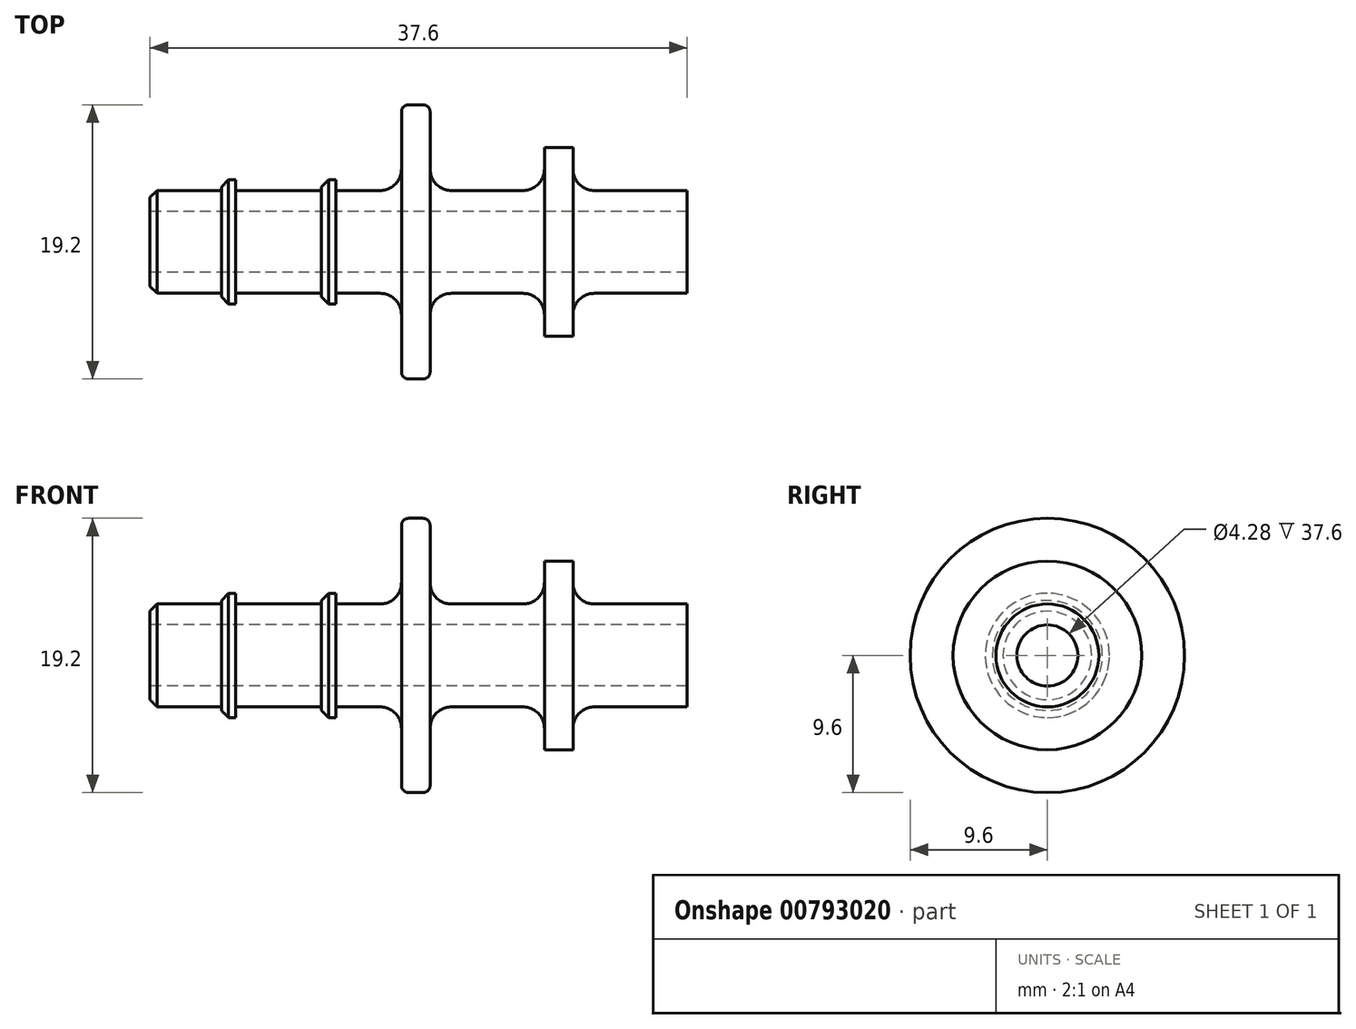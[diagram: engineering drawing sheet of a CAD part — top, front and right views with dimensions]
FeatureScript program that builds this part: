
annotation { "Feature Type Name" : "Feature", "Feature Type Description" : "" }
export const myFeature = defineFeature(function(context is Context, id is Id, definition is map)
    precondition{}
    {
        {
            var Q0;
            Q0=qCreatedBy(makeId("Front.planeOp"),FACE);
            var sketch = newSketch(context, id + "F0", { "sketchPlane" : qUnion([Q0])});
            skLineSegment(sketch, "E0.bottom", {"start": v(-18.8, 0) * mm, "end": v(18.8, 0) * mm});
            skLineSegment(sketch, "E0.top", {"start": v(-18.8, 0) * mm, "end": v(18.8, 0) * mm});
            skLineSegment(sketch, "E0.left", {"start": v(-18.8, 0) * mm, "end": v(-18.8, 0) * mm});
            skLineSegment(sketch, "E0.right", {"start": v(18.8, 0) * mm, "end": v(18.8, 0) * mm});
            skPoint(sketch, "E0.middle", {"position": v(0, 0) * mm});
            skLineSegment(sketch, "E1", {"start": v(18.8, 0) * mm, "end": v(18.8, 3.6) * mm});
            skLineSegment(sketch, "E2", {"start": v(18.8, 3.6) * mm, "end": v(12.3, 3.6) * mm});
            skLineSegment(sketch, "E3", {"start": v(10.8, 5.1) * mm, "end": v(10.8, 6.6) * mm});
            skLineSegment(sketch, "E4", {"start": v(10.8, 6.6) * mm, "end": v(8.8, 6.6) * mm});
            skLineSegment(sketch, "E5", {"start": v(8.8, 6.6) * mm, "end": v(8.8, 5.1) * mm});
            skLineSegment(sketch, "E6", {"start": v(7.3, 3.6) * mm, "end": v(2.3, 3.6) * mm});
            skLineSegment(sketch, "E7", {"start": v(0.8, 5.1) * mm, "end": v(0.8, 9.1) * mm});
            skLineSegment(sketch, "E8", {"start": v(0.3, 9.6) * mm, "end": v(-0.7, 9.6) * mm});
            skLineSegment(sketch, "E9", {"start": v(-1.2, 9.1) * mm, "end": v(-1.2, 5.1) * mm});
            skLineSegment(sketch, "E10", {"start": v(-2.7, 3.6) * mm, "end": v(-5.8, 3.6) * mm});
            skLineSegment(sketch, "E11", {"start": v(-5.8, 3.6) * mm, "end": v(-5.8, 4.35) * mm});
            skLineSegment(sketch, "E12", {"start": v(-5.8, 4.35) * mm, "end": v(-6.8, 4.35) * mm});
            skLineSegment(sketch, "E13", {"start": v(-6.8, 4.35) * mm, "end": v(-6.8, 3.6) * mm});
            skLineSegment(sketch, "E14", {"start": v(-6.8, 3.6) * mm, "end": v(-12.8, 3.6) * mm});
            skLineSegment(sketch, "E15", {"start": v(-12.8, 3.6) * mm, "end": v(-12.8, 4.35) * mm});
            skLineSegment(sketch, "E16", {"start": v(-12.8, 4.35) * mm, "end": v(-13.8, 4.35) * mm});
            skLineSegment(sketch, "E17", {"start": v(-13.8, 4.35) * mm, "end": v(-13.8, 3.6) * mm});
            skLineSegment(sketch, "E18", {"start": v(-13.8, 3.6) * mm, "end": v(-18.8, 3.6) * mm});
            skLineSegment(sketch, "E19", {"start": v(-18.8, 3.6) * mm, "end": v(-18.8, 0) * mm});
            skPoint(sketch, "E20.visualSharp", {"position": v(0.8, 9.6) * mm});
            skArc(sketch, "E20.filletArc", {"start": v(0.8, 9.1) * mm, "mid": v(0.65, 9.45) * mm, "end": v(0.3, 9.6) * mm});
            skPoint(sketch, "E21.visualSharp", {"position": v(-1.2, 9.6) * mm});
            skArc(sketch, "E21.filletArc", {"start": v(-0.7, 9.6) * mm, "mid": v(-1.05, 9.45) * mm, "end": v(-1.2, 9.1) * mm});
            skPoint(sketch, "E22.visualSharp", {"position": v(0.8, 3.6) * mm});
            skArc(sketch, "E22.filletArc", {"start": v(0.8, 5.1) * mm, "mid": v(1.24, 4.04) * mm, "end": v(2.3, 3.6) * mm});
            skPoint(sketch, "E23.visualSharp", {"position": v(-1.2, 3.6) * mm});
            skArc(sketch, "E23.filletArc", {"start": v(-2.7, 3.6) * mm, "mid": v(-1.64, 4.04) * mm, "end": v(-1.2, 5.1) * mm});
            skPoint(sketch, "E24.visualSharp", {"position": v(10.8, 3.6) * mm});
            skArc(sketch, "E24.filletArc", {"start": v(10.8, 5.1) * mm, "mid": v(11.24, 4.04) * mm, "end": v(12.3, 3.6) * mm});
            skPoint(sketch, "E25.visualSharp", {"position": v(8.8, 3.6) * mm});
            skArc(sketch, "E25.filletArc", {"start": v(7.3, 3.6) * mm, "mid": v(8.36, 4.04) * mm, "end": v(8.8, 5.1) * mm});
            skLineSegment(sketch, "E26.MirrorCS", {"start": v(18.8, 0) * mm, "end": v(18.8, -3.6) * mm});
            skLineSegment(sketch, "E27.MirrorCS", {"start": v(18.8, -3.6) * mm, "end": v(12.3, -3.6) * mm});
            skArc(sketch, "E28.MirrorCS", {"start": v(10.8, -5.1) * mm, "mid": v(11.24, -4.04) * mm, "end": v(12.3, -3.6) * mm});
            skLineSegment(sketch, "E29.MirrorCS", {"start": v(10.8, -5.1) * mm, "end": v(10.8, -6.6) * mm});
            skLineSegment(sketch, "E30.MirrorCS", {"start": v(10.8, -6.6) * mm, "end": v(8.8, -6.6) * mm});
            skLineSegment(sketch, "E31.MirrorCS", {"start": v(8.8, -6.6) * mm, "end": v(8.8, -5.1) * mm});
            skArc(sketch, "E32.MirrorCS", {"start": v(7.3, -3.6) * mm, "mid": v(8.36, -4.04) * mm, "end": v(8.8, -5.1) * mm});
            skLineSegment(sketch, "E33.MirrorCS", {"start": v(7.3, -3.6) * mm, "end": v(2.3, -3.6) * mm});
            skArc(sketch, "E34.MirrorCS", {"start": v(0.8, -5.1) * mm, "mid": v(1.24, -4.04) * mm, "end": v(2.3, -3.6) * mm});
            skLineSegment(sketch, "E35.MirrorCS", {"start": v(0.8, -5.1) * mm, "end": v(0.8, -9.1) * mm});
            skArc(sketch, "E36.MirrorCS", {"start": v(0.8, -9.1) * mm, "mid": v(0.65, -9.45) * mm, "end": v(0.3, -9.6) * mm});
            skLineSegment(sketch, "E37.MirrorCS", {"start": v(0.3, -9.6) * mm, "end": v(-0.7, -9.6) * mm});
            skArc(sketch, "E38.MirrorCS", {"start": v(-0.7, -9.6) * mm, "mid": v(-1.05, -9.45) * mm, "end": v(-1.2, -9.1) * mm});
            skLineSegment(sketch, "E39.MirrorCS", {"start": v(-1.2, -9.1) * mm, "end": v(-1.2, -5.1) * mm});
            skArc(sketch, "E40.MirrorCS", {"start": v(-2.7, -3.6) * mm, "mid": v(-1.64, -4.04) * mm, "end": v(-1.2, -5.1) * mm});
            skLineSegment(sketch, "E41.MirrorCS", {"start": v(-2.7, -3.6) * mm, "end": v(-5.8, -3.6) * mm});
            skLineSegment(sketch, "E42.MirrorCS", {"start": v(-5.8, -3.6) * mm, "end": v(-5.8, -4.35) * mm});
            skLineSegment(sketch, "E43.MirrorCS", {"start": v(-5.8, -4.35) * mm, "end": v(-6.8, -4.35) * mm});
            skLineSegment(sketch, "E44.MirrorCS", {"start": v(-6.8, -4.35) * mm, "end": v(-6.8, -3.6) * mm});
            skLineSegment(sketch, "E45.MirrorCS", {"start": v(-6.8, -3.6) * mm, "end": v(-12.8, -3.6) * mm});
            skLineSegment(sketch, "E46.MirrorCS", {"start": v(-12.8, -3.6) * mm, "end": v(-12.8, -4.35) * mm});
            skLineSegment(sketch, "E47.MirrorCS", {"start": v(-12.8, -4.35) * mm, "end": v(-13.8, -4.35) * mm});
            skLineSegment(sketch, "E48.MirrorCS", {"start": v(-13.8, -4.35) * mm, "end": v(-13.8, -3.6) * mm});
            skLineSegment(sketch, "E49.MirrorCS", {"start": v(-13.8, -3.6) * mm, "end": v(-18.8, -3.6) * mm});
            skLineSegment(sketch, "E50.MirrorCS", {"start": v(-18.8, -3.6) * mm, "end": v(-18.8, 0) * mm});
            skLineSegment(sketch, "E51", {"start": v(-18.8, 2.14) * mm, "end": v(18.8, 2.14) * mm});
            skLineSegment(sketch, "E52", {"start": v(-18.8, -2.36) * mm, "end": v(18.8, -2.36) * mm});
            skSolve(sketch);
        }
        {
            var Q0;
            {var subQ3=sQuery(id+"F0.wireOp",EDGE,"E2");Q0=makeQuery(id+"F0.imprint","IMPRINT",FACE,{"disambiguationData":[TD([[makeQuery(id+"F0.imprint","IMPRINT",EDGE,{"derivedFrom":subQ3}),1.0]])]});}
            var Q1;
            Q1=sQuery(id+"F0.wireOp",EDGE,"E0.top");
            revolve(context, id + "F1", {"surfaceOperationType" : NewSurfaceOperationType.NEW, "entities" : qUnion([Q0]), "axis" : qUnion([Q1]), "revolveType" : RevolveType.FULL});
        }
        {
            var Q0;
            Q0=makeQuery(id+"F1.opRevolve","SWEPT_EDGE",EDGE,{"disambiguationData":[OSD([sQuery(id+"F0.wireOp",EDGE,"E18"),sQuery(id+"F0.wireOp",EDGE,"E19")])]});
            var Q1;
            Q1=makeQuery(id+"F1.opRevolve","SWEPT_EDGE",EDGE,{"disambiguationData":[OSD([sQuery(id+"F0.wireOp",EDGE,"E16"),sQuery(id+"F0.wireOp",EDGE,"E17")])]});
            var Q2;
            Q2=makeQuery(id+"F1.opRevolve","SWEPT_EDGE",EDGE,{"disambiguationData":[OSD([sQuery(id+"F0.wireOp",EDGE,"E12"),sQuery(id+"F0.wireOp",EDGE,"E13")])]});
            chamfer(context, id + "F2", {"entities" : qUnion([Q0, Q1, Q2]), "width" : 0.5 * mm});
        }
    });
